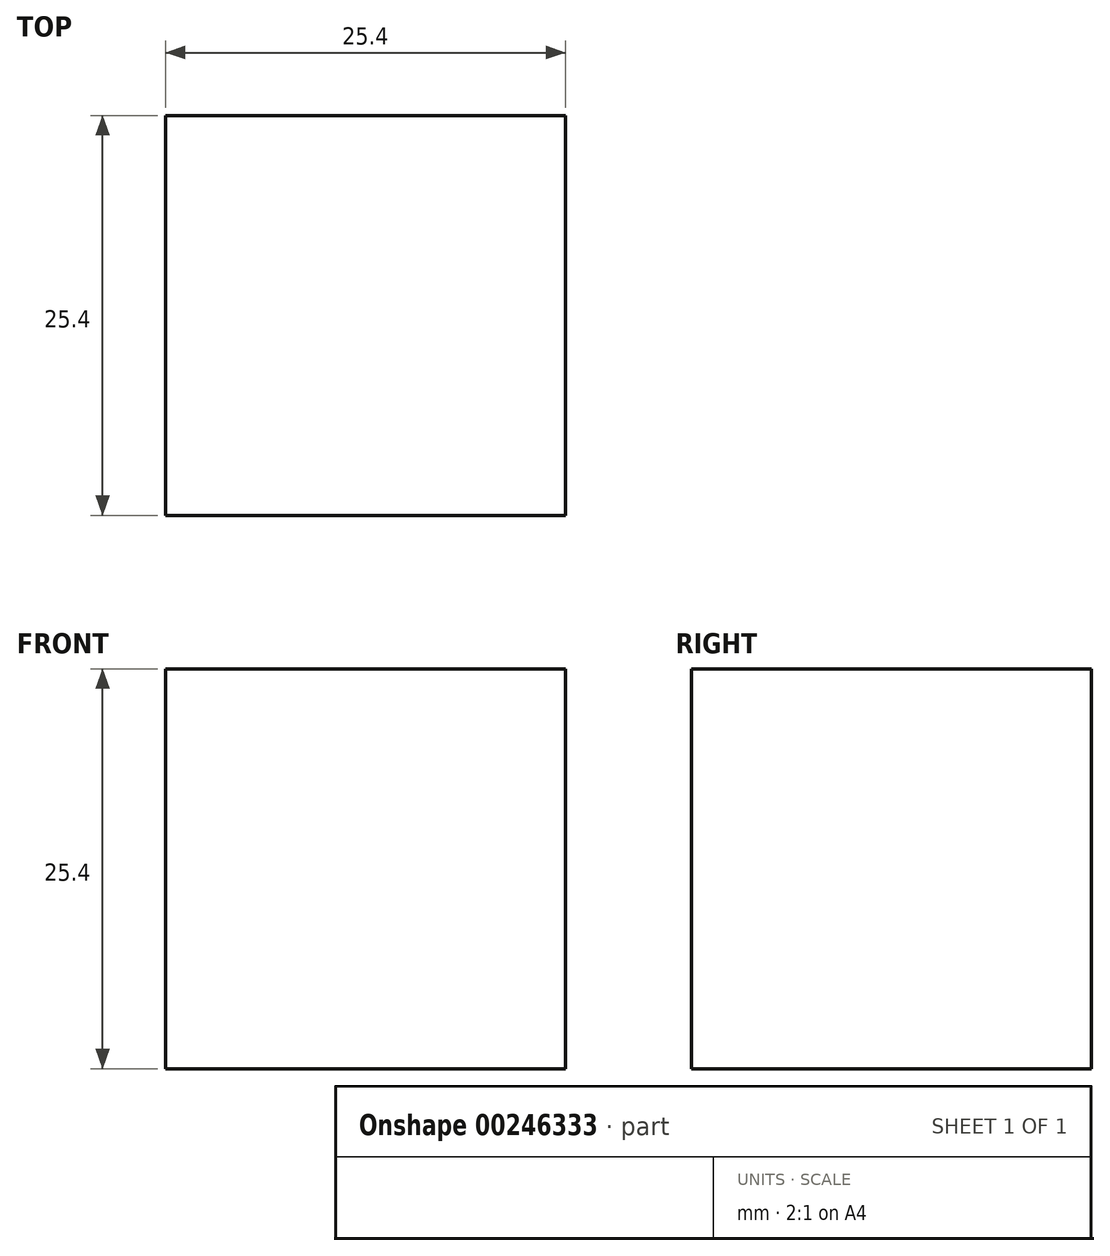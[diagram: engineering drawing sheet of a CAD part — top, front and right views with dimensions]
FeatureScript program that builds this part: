
annotation { "Feature Type Name" : "Feature", "Feature Type Description" : "" }
export const myFeature = defineFeature(function(context is Context, id is Id, definition is map)
    precondition{}
    {
        {
            var Q0;
            Q0=qCreatedBy(makeId("Front.planeOp"),FACE);
            var sketch = newSketch(context, id + "F0", { "sketchPlane" : qUnion([Q0])});
            skLineSegment(sketch, "E0.bottom", {"start": v(-54.38, 45.36) * mm, "end": v(-28.98, 45.36) * mm});
            skLineSegment(sketch, "E0.top", {"start": v(-54.38, 19.96) * mm, "end": v(-28.98, 19.96) * mm});
            skLineSegment(sketch, "E0.left", {"start": v(-54.38, 45.36) * mm, "end": v(-54.38, 19.96) * mm});
            skLineSegment(sketch, "E0.right", {"start": v(-28.98, 45.36) * mm, "end": v(-28.98, 19.96) * mm});
            skSolve(sketch);
        }
        {
            var Q0;
            Q0 = qSketchRegion(id + "F0", true);
            extrude(context, id + "F1", {"entities" : qUnion([Q0]), "depth" : 25.4 * mm});
        }
    });
